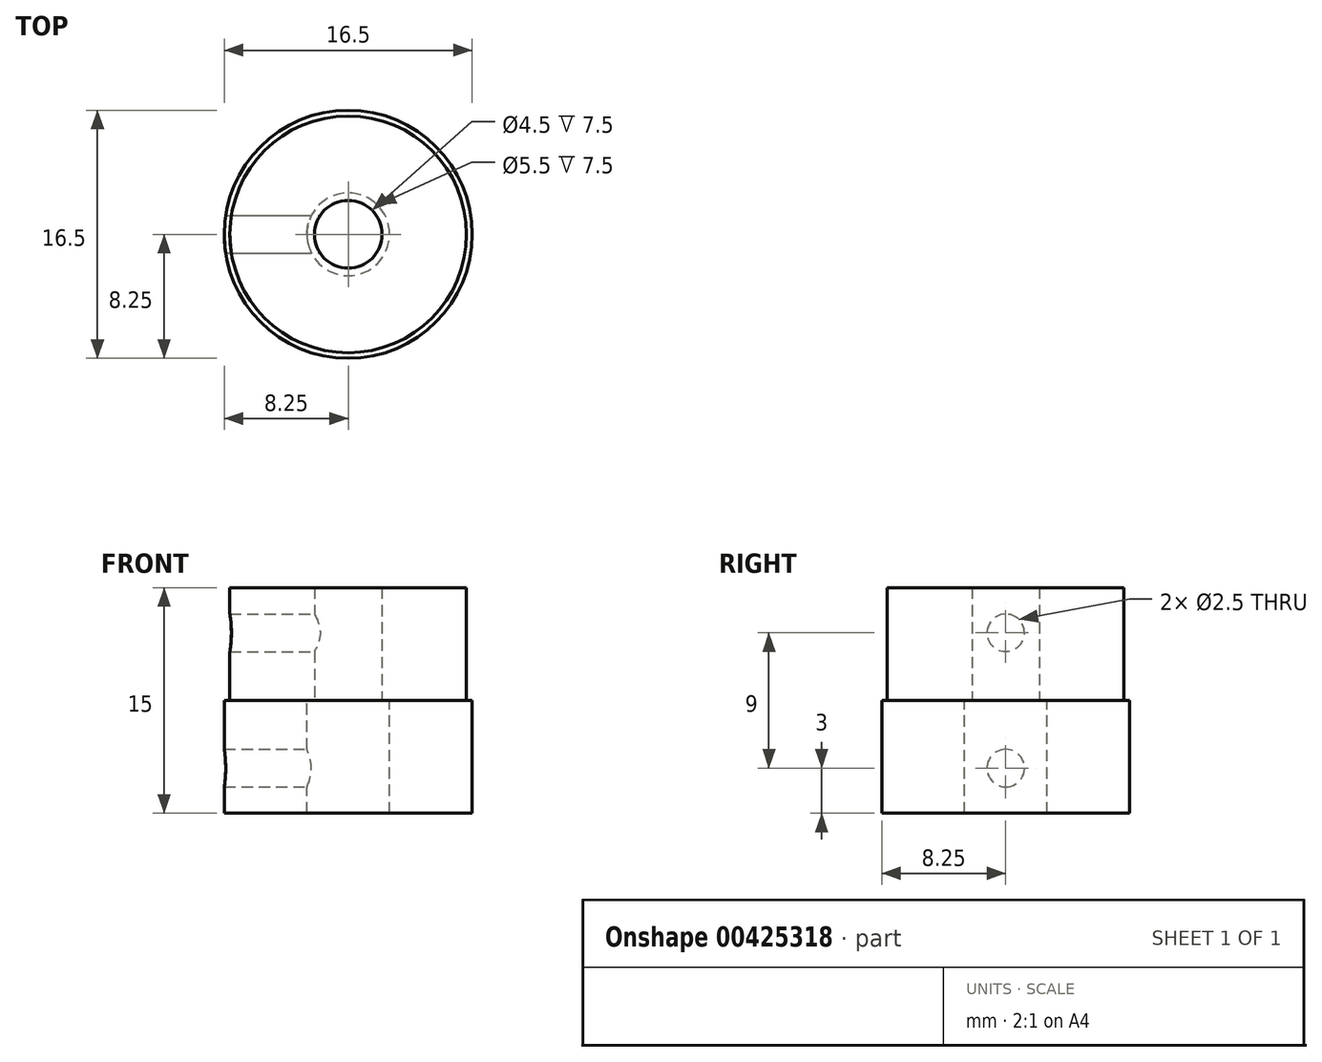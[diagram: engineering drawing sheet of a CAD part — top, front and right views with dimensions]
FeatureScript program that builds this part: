
annotation { "Feature Type Name" : "Feature", "Feature Type Description" : "" }
export const myFeature = defineFeature(function(context is Context, id is Id, definition is map)
    precondition{}
    {
        {
            var Q0;
            Q0=qCreatedBy(makeId("Top.planeOp"),FACE);
            var sketch = newSketch(context, id + "F0", { "sketchPlane" : qUnion([Q0])});
            skCircle(sketch, "E0", {"center": v(0, 0) * mm, "radius": 7.88 * mm});
            skCircle(sketch, "E1", {"center": v(0, 0) * mm, "radius": 2.25 * mm});
            skSolve(sketch);
        }
        {
            var Q0;
            Q0 = qSketchRegion(id + "F0", true);
            extrude(context, id + "F1", {"entities" : qUnion([Q0]), "depth" : 7.5 * mm});
        }
        {
            var Q0;
            Q0=makeQuery(id+"F1.opExtrude","CAP_FACE",FACE,{"disambiguationData":[OSD([sQuery(id+"F0.wireOp",EDGE,"E0"),sQuery(id+"F0.wireOp",EDGE,"E1")])],"isStart":true});
            var sketch = newSketch(context, id + "F2", { "sketchPlane" : qUnion([Q0])});
            skCircle(sketch, "E2", {"center": v(0, 0) * mm, "radius": 2.75 * mm});
            skCircle(sketch, "E3", {"center": v(0, 0) * mm, "radius": 8.25 * mm});
            skSolve(sketch);
        }
        {
            var Q0;
            Q0 = qSketchRegion(id + "F2", true);
            extrude(context, id + "F3", {"entities" : qUnion([Q0]), "operationType" : NewBodyOperationType.ADD, "depth" : 7.5 * mm});
        }
        {
            var Q0;
            Q0=qCreatedBy(makeId("Right.planeOp"),FACE);
            var sketch = newSketch(context, id + "F4", { "sketchPlane" : qUnion([Q0])});
            skCircle(sketch, "E4", {"center": v(0, 4.5) * mm, "radius": 1.25 * mm});
            skCircle(sketch, "E5", {"center": v(0, -4.5) * mm, "radius": 1.25 * mm});
            skSolve(sketch);
        }
        {
            var Q0;
            Q0 = qSketchRegion(id + "F4", true);
            extrude(context, id + "F5", {"entities" : qUnion([Q0]), "operationType" : NewBodyOperationType.REMOVE, "oppositeDirection" : true, "depth" : 25 * mm});
        }
    });
